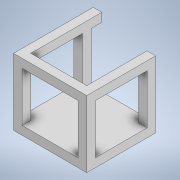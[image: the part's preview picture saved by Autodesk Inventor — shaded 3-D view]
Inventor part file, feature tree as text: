
AUTODESK INVENTOR PART (.ipt)
format: ipt  version: 2021 (Build 250183000, 183)  size: 268,800 bytes
history: native  units: in
note: dims shown in document units (in); Inventor stores cm internally (conversion verified against a paired STEP export)
features: extrude x17, sketch x17
ambient origin geometry x8: Origin, YZ Plane, XZ Plane, XY Plane, X Axis, Y Axis, Z Axis, Center Point
bodies: Solid1 (feature_tree)
feature tree (34):
  extrude  "Extrusion1"  Depth=6.6929in
  sketch  "Sketch2"  dims[d2=5.9055in d3=0.0in d4=0.7874in]
  sketch  "Sketch3"  dims[d5=0.7874in d6=0.7874in]
  extrude  "Extrusion2"  Depth=0.7874in
  extrude  "Extrusion3"  Depth=0.7874in
  extrude  "Extrusion4"  Depth=0.7874in
  extrude  "Extrusion5"  Depth=0.7874in
  extrude  "Extrusion6"  Depth=0.7874in
  extrude  "Extrusion7"  Depth=0.7874in
  sketch  "Sketch8"  dims[d15=0.7874in d16=35.4331in d17=0.0in]
  sketch  "Sketch9"  dims[d18=35.4331in d19=0.0in d20=1.5748in d21=0.0in]
  extrude  "Extrusion8"  Depth=0.7874in TaperAngle=0.0deg
  extrude  "Extrusion9"  Depth=1.5748in TaperAngle=0.0deg
  extrude  "Extrusion10"  Depth=1.5748in TaperAngle=0.0deg
  extrude  "Extrusion11"  Depth=0.3937in
  extrude  "Extrusion12"  Depth=0.7874in
  extrude  "Extrusion13"  Depth=0.7874in TaperAngle=0.0deg
  extrude  "Extrusion14"  Depth=0.3937in TaperAngle=0.0deg
  extrude  "Extrusion15"  TaperAngle=0.0deg  [1 undecoded]
  extrude  "Extrusion16"  Depth=0.1969in
  extrude  "Extrusion17"  Depth=0.9844in TaperAngle=0.0deg
  sketch  "Sketch1"  dims[d0=12.2047in d1=6.6929in]
  sketch  "Sketch4"  dims[d7=0.7874in d8=0.7874in]
  sketch  "Sketch5"  dims[d9=0.7874in d10=0.7874in]
  sketch  "Sketch6"  dims[d11=0.7874in d12=0.7874in]
  sketch  "Sketch7"  dims[d13=0.7874in d14=0.7874in]
  sketch  "Sketch10"  dims[d22=6.8898in d23=1.5748in d24=0.0in]
  sketch  "Sketch11"  dims[d25=0.3937in d26=0.0in d27=0.3937in]
  sketch  "Sketch12"  dims[d28=0.3937in d29=0.0in d30=0.7874in]
  sketch  "Sketch13"  dims[d31=0.7874in d32=0.3937in d33=0.0in]
  sketch  "Sketch14"  dims[d34=0.3937in d35=0.0in d36=0.3937in d37=0.0in]
  sketch  "Sketch15"  dims[d38=0.3937in d39=0.0in d40=0.0in]
  sketch  "Sketch17"  dims[d41=0.1969in d42=0.0in d43=0.1969in]
  sketch  "Sketch18"  dims[d44=0.1969in d45=0.0in d46=0.1969in d47=0.0in d48=0.1969in d49=0.0in d50=0.0in d52=0.7874in d53=0.9844in d54=0.0in d55=0.9844in d56=0.0in]
note: 1 required parameter value undecoded (feature->parameter linkage not recoverable at this tier; creation-order binding heuristic only, values carry confidence <= 0.55)
